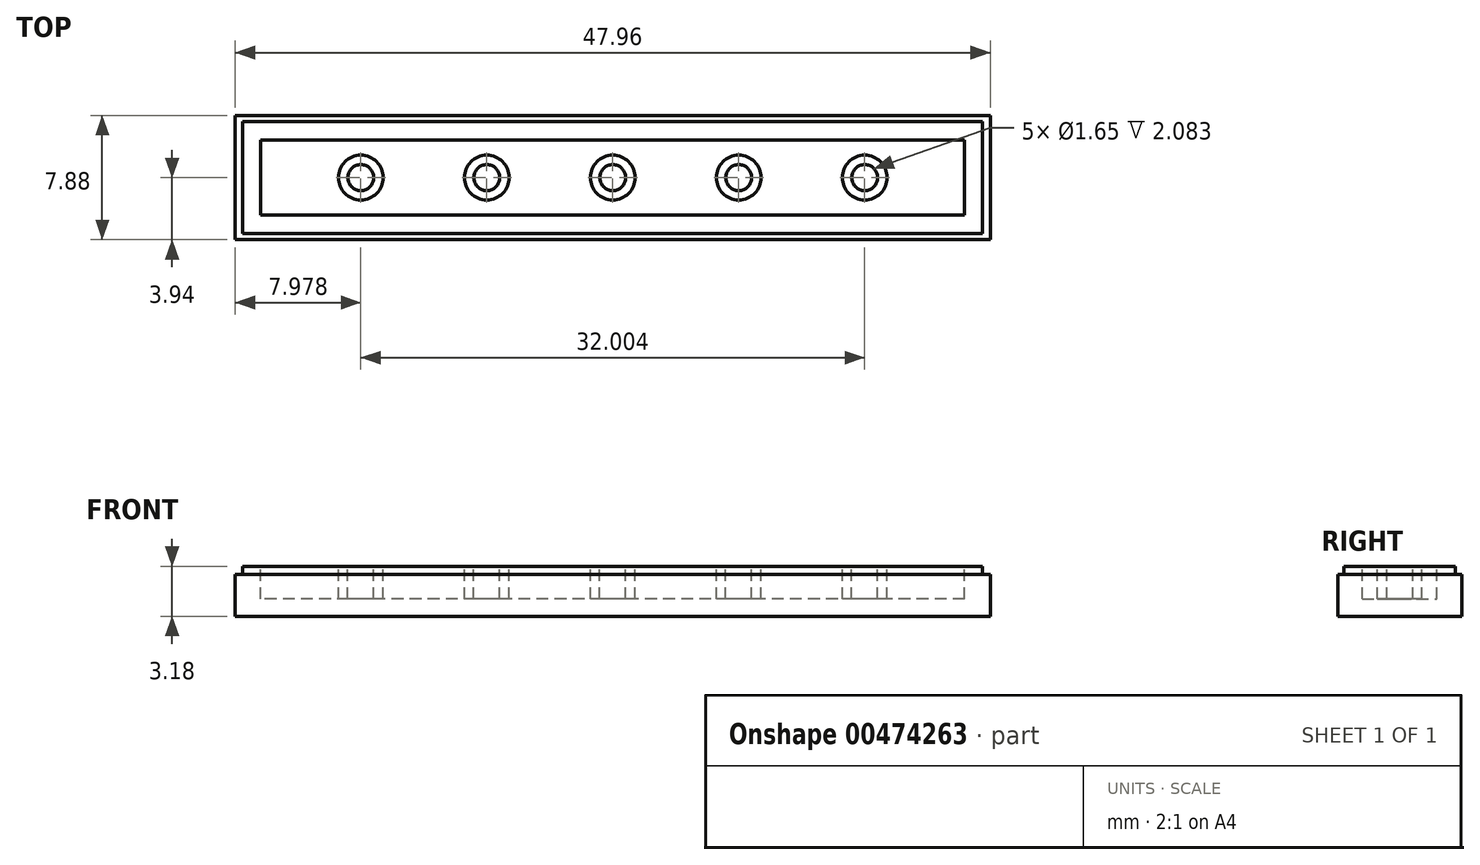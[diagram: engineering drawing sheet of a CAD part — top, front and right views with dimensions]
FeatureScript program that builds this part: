
annotation { "Feature Type Name" : "Feature", "Feature Type Description" : "" }
export const myFeature = defineFeature(function(context is Context, id is Id, definition is map)
    precondition{}
    {
        {
            var Q0;
            Q0=qCreatedBy(makeId("Top.planeOp"),FACE);
            var sketch = newSketch(context, id + "F0", { "sketchPlane" : qUnion([Q0])});
            skLineSegment(sketch, "E0.bottom", {"start": v(23.98, -3.94) * mm, "end": v(-23.98, -3.94) * mm});
            skLineSegment(sketch, "E0.top", {"start": v(23.98, 3.94) * mm, "end": v(-23.98, 3.94) * mm});
            skLineSegment(sketch, "E0.left", {"start": v(23.98, -3.94) * mm, "end": v(23.98, 3.94) * mm});
            skLineSegment(sketch, "E0.right", {"start": v(-23.98, -3.94) * mm, "end": v(-23.98, 3.94) * mm});
            skPoint(sketch, "E0.middle", {"position": v(0, 0) * mm});
            skSolve(sketch);
        }
        {
            var Q0;
            Q0=makeQuery(id+"F0.imprint","IMPRINT",FACE,{"disambiguationData":[TD([[makeQuery(id+"F0.imprint","IMPRINT",EDGE,{"derivedFrom":sQuery(id+"F0.wireOp",EDGE,"E0.bottom")}),-1.0]])]});
            extrude(context, id + "F1", {"entities" : qUnion([Q0]), "depth" : 3.17 * mm});
        }
        {
            var Q0;
            Q0=makeQuery(id+"F1.opExtrude","CAP_FACE",FACE,{"disambiguationData":[OSD([sQuery(id+"F0.wireOp",EDGE,"E0.bottom"),sQuery(id+"F0.wireOp",EDGE,"E0.top"),sQuery(id+"F0.wireOp",EDGE,"E0.left"),sQuery(id+"F0.wireOp",EDGE,"E0.right")])],"isStart":false});
            var sketch = newSketch(context, id + "F2", { "sketchPlane" : qUnion([Q0])});
            skLineSegment(sketch, "E1.bottom", {"start": v(22.35, -2.37) * mm, "end": v(-22.35, -2.37) * mm});
            skLineSegment(sketch, "E1.top", {"start": v(22.35, 2.37) * mm, "end": v(-22.35, 2.37) * mm});
            skLineSegment(sketch, "E1.left", {"start": v(22.35, -2.37) * mm, "end": v(22.35, 2.37) * mm});
            skLineSegment(sketch, "E1.right", {"start": v(-22.35, -2.37) * mm, "end": v(-22.35, 2.37) * mm});
            skPoint(sketch, "E1.middle", {"position": v(0, 0) * mm});
            skCircle(sketch, "E2", {"center": v(0, 0) * mm, "radius": 1.42 * mm});
            skCircle(sketch, "E3", {"center": v(0, 0) * mm, "radius": 0.83 * mm});
            skCircle(sketch, "E4.1.0.0", {"center": v(8, 0) * mm, "radius": 0.83 * mm});
            skCircle(sketch, "E4.1.0.1", {"center": v(8, 0) * mm, "radius": 1.42 * mm});
            skCircle(sketch, "E4.2.0.0", {"center": v(16, 0) * mm, "radius": 0.83 * mm});
            skCircle(sketch, "E4.2.0.1", {"center": v(16, 0) * mm, "radius": 1.42 * mm});
            skLineSegment(sketch, "E4.direction1", {"start": v(0, 0) * mm, "end": v(8, 0) * mm, "construction": true});
            skCircle(sketch, "E5.1.0.0", {"center": v(-8, 0) * mm, "radius": 1.42 * mm});
            skCircle(sketch, "E5.1.0.1", {"center": v(-8, 0) * mm, "radius": 0.83 * mm});
            skCircle(sketch, "E5.2.0.0", {"center": v(-16, 0) * mm, "radius": 1.42 * mm});
            skCircle(sketch, "E5.2.0.1", {"center": v(-16, 0) * mm, "radius": 0.83 * mm});
            skLineSegment(sketch, "E5.direction1", {"start": v(0, 0) * mm, "end": v(-8, 0) * mm, "construction": true});
            skSolve(sketch);
        }
        {
            var Q0;
            Q0 = qSketchRegion(id + "F2", true);
            extrude(context, id + "F3", {"entities" : qUnion([Q0]), "operationType" : NewBodyOperationType.REMOVE, "oppositeDirection" : true, "depth" : 2.08 * mm});
        }
        {
            var Q0;
            Q0=makeQuery(id+"F2.imprint","IMPRINT",FACE,{"disambiguationData":[TD([[makeQuery(id+"F2.imprint","IMPRINT",EDGE,{"derivedFrom":sQuery(id+"F2.wireOp",EDGE,"E4.2.0.0")}),1.0]])]});
            var Q1;
            Q1=makeQuery(id+"F2.imprint","IMPRINT",FACE,{"disambiguationData":[TD([[makeQuery(id+"F2.imprint","IMPRINT",EDGE,{"derivedFrom":sQuery(id+"F2.wireOp",EDGE,"E4.1.0.0")}),1.0]])]});
            var Q2;
            Q2=makeQuery(id+"F2.imprint","IMPRINT",FACE,{"disambiguationData":[TD([[makeQuery(id+"F2.imprint","IMPRINT",EDGE,{"derivedFrom":sQuery(id+"F2.wireOp",EDGE,"E5.1.0.1")}),1.0]])]});
            var Q3;
            Q3=makeQuery(id+"F2.imprint","IMPRINT",FACE,{"disambiguationData":[TD([[makeQuery(id+"F2.imprint","IMPRINT",EDGE,{"derivedFrom":sQuery(id+"F2.wireOp",EDGE,"E3")}),1.0]])]});
            var Q4;
            Q4=makeQuery(id+"F2.imprint","IMPRINT",FACE,{"disambiguationData":[TD([[makeQuery(id+"F2.imprint","IMPRINT",EDGE,{"derivedFrom":sQuery(id+"F2.wireOp",EDGE,"E5.2.0.1")}),1.0]])]});
            extrude(context, id + "F4", {"entities" : qUnion([Q0, Q1, Q2, Q3, Q4]), "operationType" : NewBodyOperationType.REMOVE, "oppositeDirection" : true, "depth" : 2.08 * mm});
        }
        {
            var Q0;
            Q0=makeQuery(id+"F2.imprint","IMPRINT",FACE,{"disambiguationData":[TD([[makeQuery(id+"F2.imprint","IMPRINT",EDGE,{"derivedFrom":sQuery(id+"F2.wireOp",EDGE,"E1.bottom")}),1.0]])]});
            var sketch = newSketch(context, id + "F5", { "sketchPlane" : qUnion([Q0])});
            skLineSegment(sketch, "E6.bottom", {"start": v(23.5, -3.54) * mm, "end": v(-23.5, -3.54) * mm});
            skLineSegment(sketch, "E6.top", {"start": v(23.5, 3.54) * mm, "end": v(-23.5, 3.54) * mm});
            skLineSegment(sketch, "E6.left", {"start": v(23.5, -3.54) * mm, "end": v(23.5, 3.54) * mm});
            skLineSegment(sketch, "E6.right", {"start": v(-23.5, -3.54) * mm, "end": v(-23.5, 3.54) * mm});
            skPoint(sketch, "E6.middle", {"position": v(0, 0) * mm});
            skLineSegment(sketch, "E7.bottom", {"start": v(24.54, 4.68) * mm, "end": v(-24.54, 4.68) * mm});
            skLineSegment(sketch, "E7.top", {"start": v(24.54, -4.68) * mm, "end": v(-24.54, -4.68) * mm});
            skLineSegment(sketch, "E7.left", {"start": v(24.54, 4.68) * mm, "end": v(24.54, -4.68) * mm});
            skLineSegment(sketch, "E7.right", {"start": v(-24.54, 4.68) * mm, "end": v(-24.54, -4.68) * mm});
            skSolve(sketch);
        }
        {
            var Q0;
            Q0 = qSketchRegion(id + "F5", true);
            extrude(context, id + "F6", {"entities" : qUnion([Q0]), "operationType" : NewBodyOperationType.REMOVE, "oppositeDirection" : true, "depth" : 0.5 * mm});
        }
    });
